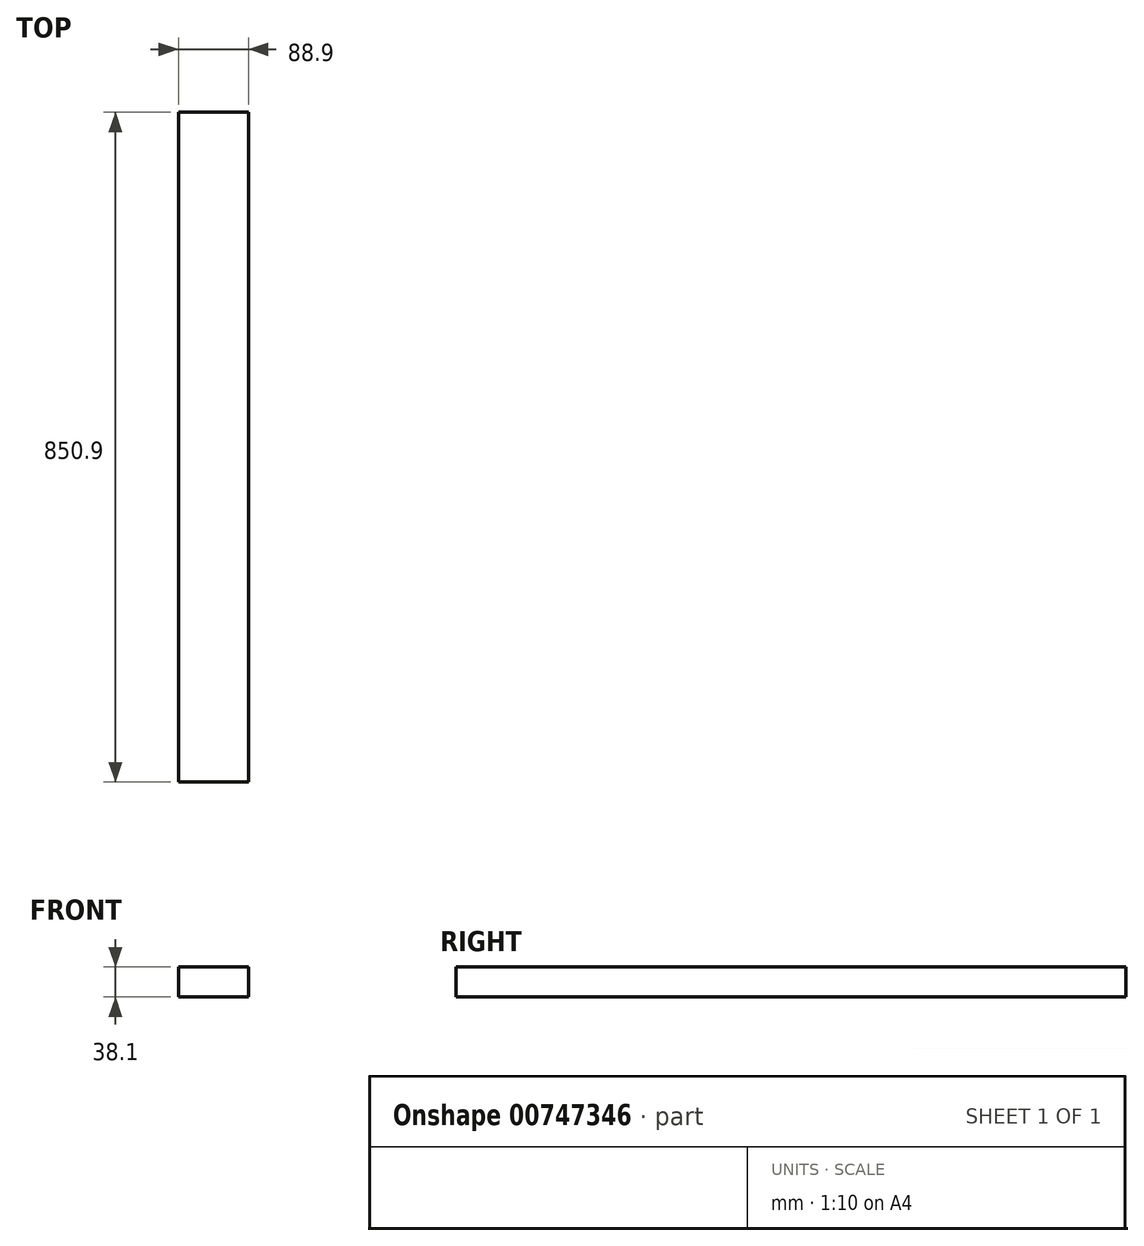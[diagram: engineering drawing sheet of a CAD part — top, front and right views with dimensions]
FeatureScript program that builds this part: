
annotation { "Feature Type Name" : "Feature", "Feature Type Description" : "" }
export const myFeature = defineFeature(function(context is Context, id is Id, definition is map)
    precondition{}
    {
        {
            var Q0;
            Q0=qCreatedBy(makeId("Front.planeOp"),FACE);
            var sketch = newSketch(context, id + "F0", { "sketchPlane" : qUnion([Q0])});
            skLineSegment(sketch, "E0.bottom", {"start": v(0, 0) * mm, "end": v(88.9, 0) * mm});
            skLineSegment(sketch, "E0.top", {"start": v(0, 38.1) * mm, "end": v(88.9, 38.1) * mm});
            skLineSegment(sketch, "E0.left", {"start": v(0, 0) * mm, "end": v(0, 38.1) * mm});
            skLineSegment(sketch, "E0.right", {"start": v(88.9, 0) * mm, "end": v(88.9, 38.1) * mm});
            skSolve(sketch);
        }
        {
            var Q0;
            Q0=qSketchRegion(id+"F0",true);
            extrude(context, id + "F1", {"entities" : qUnion([Q0]), "depth" : 850.9 * mm, "offsetDistance" : 25.4 * mm});
        }
    });
